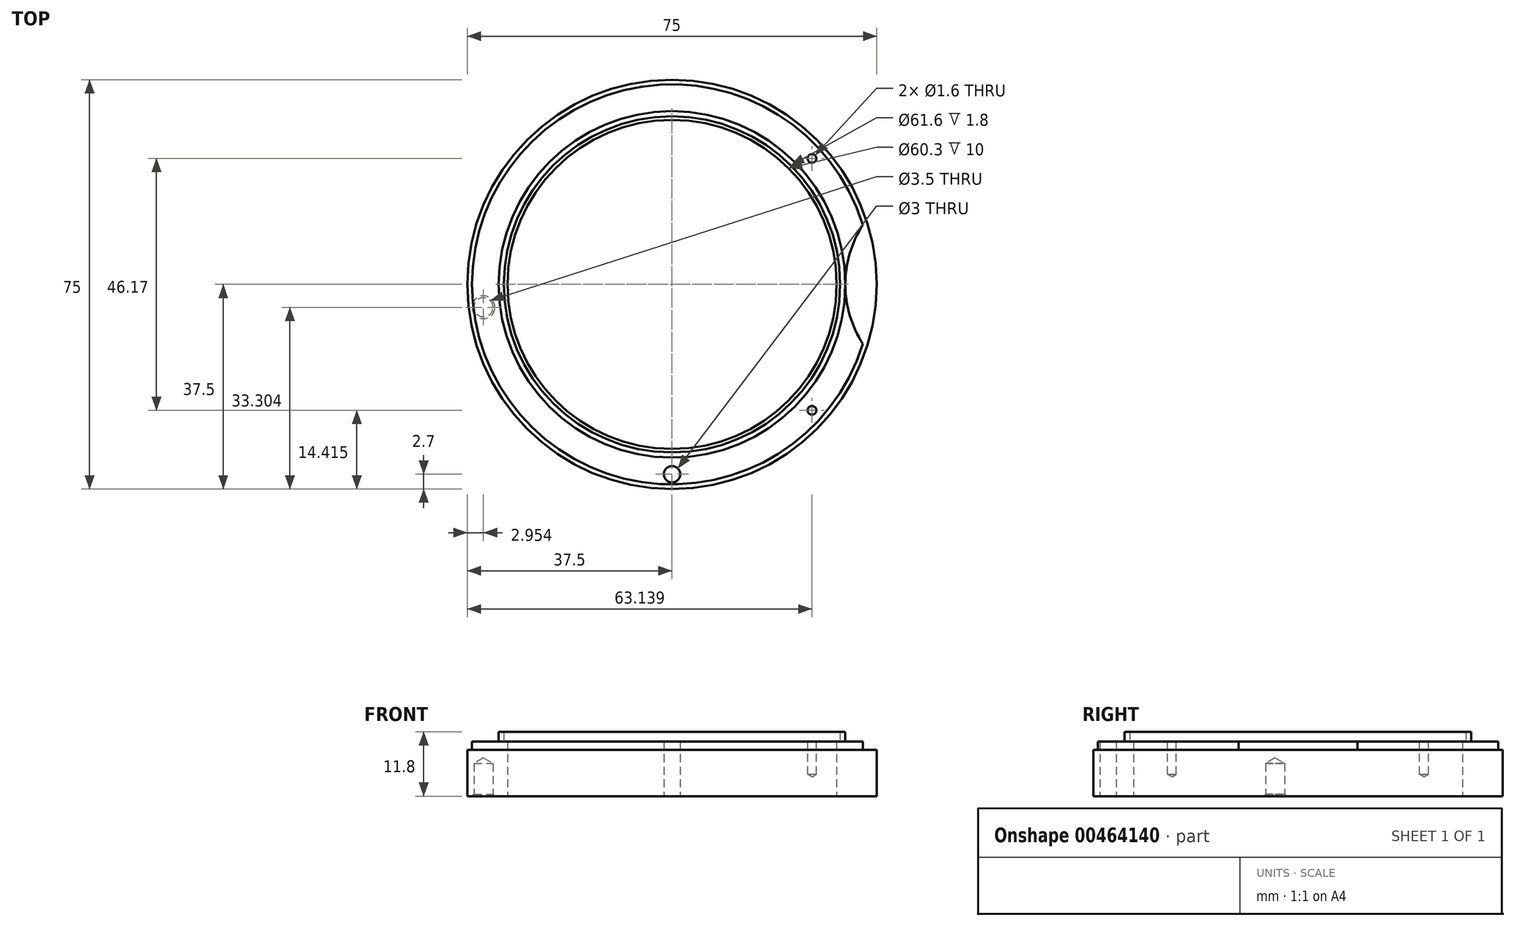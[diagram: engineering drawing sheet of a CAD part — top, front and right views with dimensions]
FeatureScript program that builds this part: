
annotation { "Feature Type Name" : "Feature", "Feature Type Description" : "" }
export const myFeature = defineFeature(function(context is Context, id is Id, definition is map)
    precondition{}
    {
        {
            var Q0;
            Q0=qCreatedBy(makeId("Top.planeOp"),FACE);
            var sketch = newSketch(context, id + "F0", { "sketchPlane" : qUnion([Q0])});
            skCircle(sketch, "E0", {"center": v(0, 0) * mm, "radius": 37.5 * mm});
            skCircle(sketch, "E1", {"center": v(0, 0) * mm, "radius": 36.65 * mm});
            skCircle(sketch, "E2", {"center": v(0, 0) * mm, "radius": 34.5 * mm, "construction": true});
            skCircle(sketch, "E3", {"center": v(0, 0) * mm, "radius": 31.75 * mm});
            skCircle(sketch, "E4", {"center": v(0, 0) * mm, "radius": 30.8 * mm});
            skCircle(sketch, "E5", {"center": v(0, 0) * mm, "radius": 30.15 * mm});
            skSolve(sketch);
        }
        {
            var Q0;
            Q0=makeQuery(id+"F0.imprint","IMPRINT",FACE,{"disambiguationData":[TD([[makeQuery(id+"F0.imprint","IMPRINT",EDGE,{"derivedFrom":sQuery(id+"F0.wireOp",EDGE,"E3")}),1.0]])]});
            extrude(context, id + "F1", {"entities" : qUnion([Q0]), "depth" : 11.8 * mm});
        }
        {
            var Q0;
            Q0=makeQuery(id+"F0.imprint","IMPRINT",FACE,{"disambiguationData":[TD([[makeQuery(id+"F0.imprint","IMPRINT",EDGE,{"derivedFrom":sQuery(id+"F0.wireOp",EDGE,"E4")}),1.0]])]});
            var Q1;
            Q1=makeQuery(id+"F0.imprint","IMPRINT",FACE,{"disambiguationData":[TD([[makeQuery(id+"F0.imprint","IMPRINT",EDGE,{"derivedFrom":sQuery(id+"F0.wireOp",EDGE,"E1")}),1.0]])]});
            extrude(context, id + "F2", {"entities" : qUnion([Q0, Q1]), "operationType" : NewBodyOperationType.ADD, "depth" : 10 * mm});
        }
        {
            var Q0;
            Q0=makeQuery(id+"F0.imprint","IMPRINT",FACE,{"disambiguationData":[TD([[makeQuery(id+"F0.imprint","IMPRINT",EDGE,{"derivedFrom":sQuery(id+"F0.wireOp",EDGE,"E0")}),1.0]])]});
            extrude(context, id + "F3", {"entities" : qUnion([Q0]), "operationType" : NewBodyOperationType.ADD, "depth" : 8.5 * mm});
        }
        {
            var Q0;
            Q0=makeQuery(id+"F2.opExtrude","CAP_FACE",FACE,{"disambiguationData":[OSD([sQuery(id+"F0.wireOp",EDGE,"E1"),sQuery(id+"F0.wireOp",EDGE,"E3")])],"isStart":false});
            var sketch = newSketch(context, id + "F4", { "sketchPlane" : qUnion([Q0])});
            skPoint(sketch, "E6.0", {"position": v(0, 0) * mm});
            skCircle(sketch, "E7.0", {"center": v(0, 0) * mm, "radius": 34.5 * mm, "construction": true});
            skLineSegment(sketch, "E8", {"start": v(0, 0) * mm, "end": v(25.64, -23.09) * mm, "construction": true});
            skLineSegment(sketch, "E9", {"start": v(0, 0) * mm, "end": v(25.64, 23.09) * mm, "construction": true});
            skPoint(sketch, "E10", {"position": v(51.75, 0) * mm});
            skArc(sketch, "E11", {"start": v(34.99, 10.91) * mm, "mid": v(31.75, 0) * mm, "end": v(34.99, -10.91) * mm});
            skCircle(sketch, "E12.0", {"center": v(0, 0) * mm, "radius": 36.65 * mm});
            skSolve(sketch);
        }
        {
            var Q0;
            Q0=sQuery(id+"F4.wireOp",VERTEX,"E8.end");
            var Q1;
            Q1=makeQuery(id+"F1.opExtrude","SWEPT_BODY",BODY,{"disambiguationData":[OSD([sQuery(id+"F0.wireOp",EDGE,"E3"),sQuery(id+"F0.wireOp",EDGE,"E4")])]});
            hole(context, id + "F5", {"style" : HoleStyle.SIMPLE, "endStyle" : HoleEndStyle.BLIND, "holeDiameter" : 1.6 * mm, "holeDepth" : 6 * mm, "isTappedThrough" : true, "tappedDepth" : 100 * mm, "tapClearance" : 3, "startFromSketch" : true, "locations" : qUnion([Q0]), "scope" : qUnion([Q1])});
        }
        {
            var Q0;
            Q0=sQuery(id+"F4.wireOp",VERTEX,"E9.end");
            var Q1;
            Q1=makeQuery(id+"F1.opExtrude","SWEPT_BODY",BODY,{"disambiguationData":[OSD([sQuery(id+"F0.wireOp",EDGE,"E3"),sQuery(id+"F0.wireOp",EDGE,"E4")])]});
            hole(context, id + "F6", {"style" : HoleStyle.SIMPLE, "endStyle" : HoleEndStyle.BLIND, "holeDiameter" : 1.6 * mm, "holeDepth" : 6 * mm, "isTappedThrough" : true, "tappedDepth" : 100 * mm, "tapClearance" : 3, "startFromSketch" : true, "locations" : qUnion([Q0]), "scope" : qUnion([Q1])});
        }
        {
            var Q0;
            {var subQ0=sQuery(id+"F4.wireOp",EDGE,"E12.0");var subQ1=sQuery(id+"F4.wireOp",EDGE,"E11");var subQ2=makeQuery(id+"F4.imprint","INTERSECT",VERTEX,{"disambiguationData":[OD(0.0)],"derivedFrom":[subQ1,subQ0]});Q0=makeQuery(id+"F4.imprint","IMPRINT",FACE,{"disambiguationData":[TD([[makeQuery(id+"F4.imprint","IMPRINT",EDGE,{"disambiguationData":[TD([[subQ2,-1.0]])],"derivedFrom":subQ1}),1.0]])]});}
            var Q1;
            Q1=makeQuery(id+"F3.opExtrude","CAP_FACE",FACE,{"disambiguationData":[OSD([sQuery(id+"F0.wireOp",EDGE,"E0"),sQuery(id+"F0.wireOp",EDGE,"E1")])],"isStart":false});
            extrude(context, id + "F7", {"entities" : qUnion([Q0]), "operationType" : NewBodyOperationType.REMOVE, "endBound" : BoundingType.UP_TO_SURFACE, "oppositeDirection" : true, "endBoundEntityFace" : qUnion([Q1]), "depth" : 25 * mm});
        }
        {
            var Q0;
            Q0=qCreatedBy(makeId("Top.planeOp"),FACE);
            var sketch = newSketch(context, id + "F8", { "sketchPlane" : qUnion([Q0])});
            skPoint(sketch, "E13.0", {"position": v(0, 0) * mm});
            skCircle(sketch, "E14", {"center": v(0, 0) * mm, "radius": 34.8 * mm, "construction": true});
            skLineSegment(sketch, "E15", {"start": v(0, 0) * mm, "end": v(-34.55, -4.2) * mm, "construction": true});
            skPoint(sketch, "E16", {"position": v(0, -34.8) * mm});
            skSolve(sketch);
        }
        {
            var Q0;
            Q0=sQuery(id+"F8.wireOp",VERTEX,"E15.end");
            var Q1;
            Q1=makeQuery(id+"F1.opExtrude","SWEPT_BODY",BODY,{"disambiguationData":[OSD([sQuery(id+"F0.wireOp",EDGE,"E3"),sQuery(id+"F0.wireOp",EDGE,"E4")])]});
            hole(context, id + "F9", {"style" : HoleStyle.C_SINK, "endStyle" : HoleEndStyle.BLIND, "oppositeDirection" : true, "holeDiameter" : 3.5 * mm, "cSinkDiameter" : 4.2 * mm, "cSinkAngle" : 90 * degree, "holeDepth" : 6 * mm, "isTappedThrough" : true, "tappedDepth" : 100 * mm, "tapClearance" : 3, "startFromSketch" : true, "locations" : qUnion([Q0]), "scope" : qUnion([Q1])});
        }
        {
            var Q0;
            Q0=sQuery(id+"F8.wireOp",VERTEX,"E16");
            var Q1;
            Q1=makeQuery(id+"F1.opExtrude","SWEPT_BODY",BODY,{"disambiguationData":[OSD([sQuery(id+"F0.wireOp",EDGE,"E3"),sQuery(id+"F0.wireOp",EDGE,"E4")])]});
            hole(context, id + "F10", {"style" : HoleStyle.SIMPLE, "endStyle" : HoleEndStyle.THROUGH, "oppositeDirection" : true, "holeDiameter" : 3 * mm, "isTappedThrough" : true, "tappedDepth" : 100 * mm, "tapClearance" : 3, "startFromSketch" : true, "locations" : qUnion([Q0]), "scope" : qUnion([Q1])});
        }
    });
